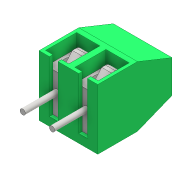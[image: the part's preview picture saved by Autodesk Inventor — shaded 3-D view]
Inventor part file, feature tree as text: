
AUTODESK INVENTOR PART (.ipt)
format: ipt  version: 2016 (Build 200138000, 138)  size: 212,480 bytes
history: native  units: mm
features: other x7, sketch x2
ambient origin geometry x8: Origin, YZ Plane, XZ Plane, XY Plane, X Axis, Y Axis, Z Axis, Center Point
bodies: Solid1 (feature_tree), Solid2 (feature_tree), Solid3 (feature_tree), Solid4 (feature_tree), Solid5 (feature_tree), Solid6 (feature_tree), Solid7 (feature_tree)
feature tree (9):
  sketch  "Sketch1"
  sketch  "Sketch2"
  other  "Enlèv. mat.-Extru.3"
  other  "Boss.-Extru.4"
  other  "Extru.-Mince1"
  other  "Répétition linéaire2"
  other  "Répétition linéaire3[1]"
  other  "Répétition linéaire3[2]"
  other  "Répétition linéaire3[3]"
